FCSTD DOCUMENT  (FreeCAD 0.16RUnknown)
Label: board_simple
License: All rights reserved
LicenseURL: http://en.wikipedia.org/wiki/All_rights_reserved
objects: Part::Part2DObjectPython×2, App::FeaturePython×2
note: 2 computed .brp shape members not serialized (recipe doc carries the construction recipe); baked Part::Feature solids carry a one-line shape summary decoded from their .brp

FEATURE [Part::Part2DObjectPython] Rectangle  label="Board"  # Draft 2D object (typed FeaturePython)
  ChamferSize = 0
  Columns = 1
  FilletRadius = 0
  Height = 50
  Length = 75
  MakeFace = true
  Rows = 1
FEATURE [App::FeaturePython] Dimension002  label="Dim Board X"  # Draft dimension (typed FeaturePython)
  Dimline = (85,0,0)
  Direction = (0,1,0)
  Distance = 50
  End = (75,50,0)
  Normal = (0,0,1)
  Start = (75,0,0)
FEATURE [App::FeaturePython] Dimension003  label="Dim Board Y"  # Draft dimension (typed FeaturePython)
  Dimline = (0,60,0)
  Direction = (1,0,0)
  Distance = 75
  End = (75,50,0)
  Normal = (0,0,1)
  Start = (0,50,0)
FEATURE [Part::Part2DObjectPython] Rectangle001  label="ForcedView"  # Draft 2D object (typed FeaturePython)
  ChamferSize = 0
  Columns = 1
  FilletRadius = 0
  Height = 75
  Length = 95
  MakeFace = true
  Placement = pos=(-5,-5,0) rot=(0,0,1;0rad)
  Rows = 1
